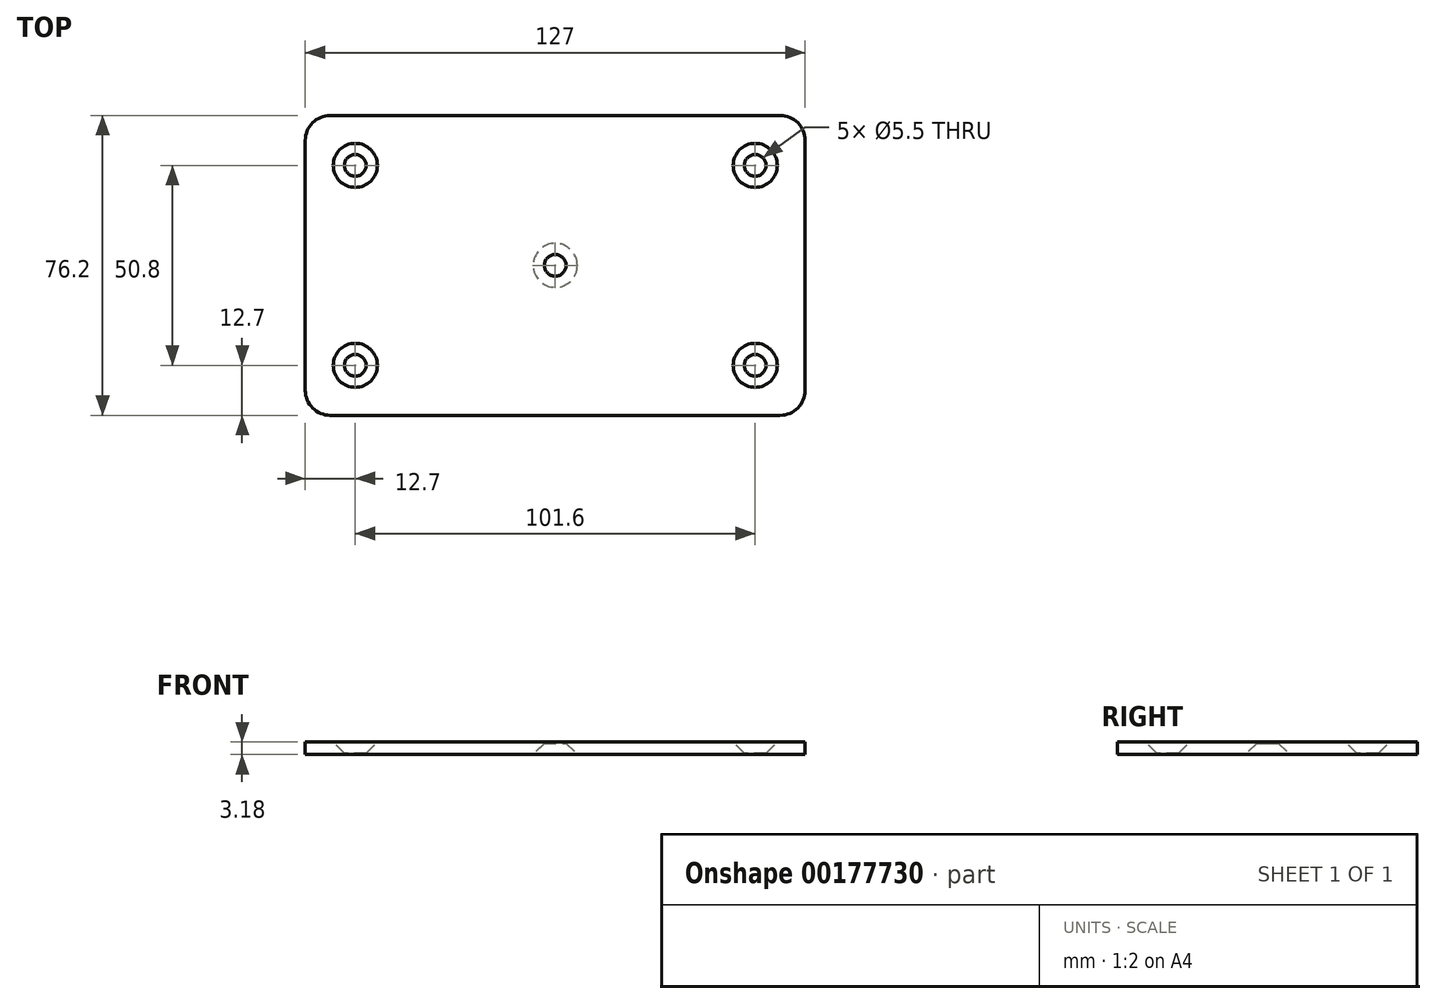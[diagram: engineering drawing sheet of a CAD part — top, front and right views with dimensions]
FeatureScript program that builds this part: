
annotation { "Feature Type Name" : "Feature", "Feature Type Description" : "" }
export const myFeature = defineFeature(function(context is Context, id is Id, definition is map)
    precondition{}
    {
        {
            var Q0;
            Q0=qCreatedBy(makeId("Top.planeOp"),FACE);
            var sketch = newSketch(context, id + "F0", { "sketchPlane" : qUnion([Q0])});
            skLineSegment(sketch, "E0.bottom", {"start": v(63.5, 38.1) * mm, "end": v(-63.5, 38.1) * mm});
            skLineSegment(sketch, "E0.top", {"start": v(63.5, -38.1) * mm, "end": v(-63.5, -38.1) * mm});
            skLineSegment(sketch, "E0.left", {"start": v(63.5, 38.1) * mm, "end": v(63.5, -38.1) * mm});
            skLineSegment(sketch, "E0.right", {"start": v(-63.5, 38.1) * mm, "end": v(-63.5, -38.1) * mm});
            skPoint(sketch, "E0.middle", {"position": v(0, 0) * mm});
            skSolve(sketch);
        }
        {
            var Q0;
            Q0=makeQuery(id+"F0.imprint","IMPRINT",FACE,{"disambiguationData":[TD([[makeQuery(id+"F0.imprint","IMPRINT",EDGE,{"derivedFrom":sQuery(id+"F0.wireOp",EDGE,"E0.bottom")}),1.0]])]});
            extrude(context, id + "F1", {"entities" : qUnion([Q0]), "oppositeDirection" : true, "depth" : 3.17 * mm});
        }
        {
            var Q0;
            Q0=makeQuery(id+"F1.opExtrude","CAP_FACE",FACE,{"disambiguationData":[OSD([sQuery(id+"F0.wireOp",EDGE,"E0.bottom"),sQuery(id+"F0.wireOp",EDGE,"E0.top"),sQuery(id+"F0.wireOp",EDGE,"E0.left"),sQuery(id+"F0.wireOp",EDGE,"E0.right")])],"isStart":true});
            var sketch = newSketch(context, id + "F2", { "sketchPlane" : qUnion([Q0])});
            skLineSegment(sketch, "E1.bottom", {"start": v(-50.8, 25.4) * mm, "end": v(50.8, 25.4) * mm});
            skLineSegment(sketch, "E1.top", {"start": v(-50.8, -25.4) * mm, "end": v(50.8, -25.4) * mm});
            skLineSegment(sketch, "E1.left", {"start": v(-50.8, 25.4) * mm, "end": v(-50.8, -25.4) * mm});
            skLineSegment(sketch, "E1.right", {"start": v(50.8, 25.4) * mm, "end": v(50.8, -25.4) * mm});
            skPoint(sketch, "E1.middle", {"position": v(0, 0) * mm});
            skSolve(sketch);
        }
        {
            var Q0;
            Q0=sQuery(id+"F2.wireOp",VERTEX,"E1.left.end");
            var Q1;
            Q1=sQuery(id+"F2.wireOp",VERTEX,"E1.left.start");
            var Q2;
            Q2=sQuery(id+"F2.wireOp",VERTEX,"E1.right.start");
            var Q3;
            Q3=sQuery(id+"F2.wireOp",VERTEX,"E1.right.end");
            var Q4;
            Q4=makeQuery(id+"F1.opExtrude","SWEPT_BODY",BODY,{"disambiguationData":[OSD([sQuery(id+"F0.wireOp",EDGE,"E0.bottom"),sQuery(id+"F0.wireOp",EDGE,"E0.top"),sQuery(id+"F0.wireOp",EDGE,"E0.left"),sQuery(id+"F0.wireOp",EDGE,"E0.right")])]});
            hole(context, id + "F3", {"style" : HoleStyle.C_SINK, "endStyle" : HoleEndStyle.THROUGH, "standardTappedOrClearance" : lookupTablePath({ "standard" : "ISO", "fit" : "Normal", "size" : "M5", "type" : "Clearance" }), "standardBlindInLast" : lookupTablePath({ "fit" : "Standard", "standard" : "ISO", "size" : "M5", "type" : "Clearance" }), "holeDiameter" : 5.5 * mm, "cSinkDiameter" : 11.2 * mm, "cSinkAngle" : 90 * degree, "locations" : qUnion([Q0, Q1, Q2, Q3]), "scope" : qUnion([Q4]), "isTappedThrough" : true});
        }
        {
            var Q0;
            Q0=makeQuery(id+"F1.opExtrude","CAP_FACE",FACE,{"disambiguationData":[OSD([sQuery(id+"F0.wireOp",EDGE,"E0.bottom"),sQuery(id+"F0.wireOp",EDGE,"E0.top"),sQuery(id+"F0.wireOp",EDGE,"E0.left"),sQuery(id+"F0.wireOp",EDGE,"E0.right")])],"isStart":false});
            var sketch = newSketch(context, id + "F4", { "sketchPlane" : qUnion([Q0])});
            skPoint(sketch, "E2", {"position": v(0, 0) * mm});
            skSolve(sketch);
        }
        {
            var Q0;
            Q0=sQuery(id+"F4.wireOp",VERTEX,"E2");
            var Q1;
            Q1=makeQuery(id+"F1.opExtrude","SWEPT_BODY",BODY,{"disambiguationData":[OSD([sQuery(id+"F0.wireOp",EDGE,"E0.bottom"),sQuery(id+"F0.wireOp",EDGE,"E0.top"),sQuery(id+"F0.wireOp",EDGE,"E0.left"),sQuery(id+"F0.wireOp",EDGE,"E0.right")])]});
            hole(context, id + "F5", {"style" : HoleStyle.C_SINK, "endStyle" : HoleEndStyle.THROUGH, "standardTappedOrClearance" : lookupTablePath({ "standard" : "ISO", "fit" : "Normal", "size" : "M5", "type" : "Clearance" }), "standardBlindInLast" : lookupTablePath({ "fit" : "Standard", "standard" : "ISO", "size" : "M5", "type" : "Clearance" }), "holeDiameter" : 5.5 * mm, "cSinkDiameter" : 11.2 * mm, "cSinkAngle" : 90 * degree, "locations" : qUnion([Q0]), "scope" : qUnion([Q1]), "isTappedThrough" : true});
        }
        {
            var Q0;
            Q0=makeQuery(id+"F1.opExtrude","SWEPT_EDGE",EDGE,{"disambiguationData":[OSD([sQuery(id+"F0.wireOp",EDGE,"E0.top"),sQuery(id+"F0.wireOp",EDGE,"E0.left")])]});
            var Q1;
            Q1=makeQuery(id+"F1.opExtrude","SWEPT_EDGE",EDGE,{"disambiguationData":[OSD([sQuery(id+"F0.wireOp",EDGE,"E0.bottom"),sQuery(id+"F0.wireOp",EDGE,"E0.left")])]});
            var Q2;
            Q2=makeQuery(id+"F1.opExtrude","SWEPT_EDGE",EDGE,{"disambiguationData":[OSD([sQuery(id+"F0.wireOp",EDGE,"E0.top"),sQuery(id+"F0.wireOp",EDGE,"E0.right")])]});
            var Q3;
            Q3=makeQuery(id+"F1.opExtrude","SWEPT_EDGE",EDGE,{"disambiguationData":[OSD([sQuery(id+"F0.wireOp",EDGE,"E0.bottom"),sQuery(id+"F0.wireOp",EDGE,"E0.right")])]});
            fillet(context, id + "F6", {"entities" : qUnion([Q0, Q1, Q2, Q3]), "radius" : 6.35 * mm, "tangentPropagation" : true, "allowEdgeOverflow" : false});
        }
    });
